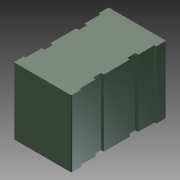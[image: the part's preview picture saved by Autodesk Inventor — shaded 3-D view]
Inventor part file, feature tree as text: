
AUTODESK INVENTOR PART (.ipt)
format: ipt  version: 2011 SP1 (Build 150282100, 282)  size: 150,016 bytes
history: native  units: in
note: dims shown in document units (in); Inventor stores cm internally (conversion verified against a paired STEP export)
features: other x21, extrude x3, sketch x3, pattern_linear x1
ambient origin geometry x8: Origin, YZ Plane, XZ Plane, XY Plane, X Axis, Y Axis, Z Axis, Center Point
bodies: Solid1 (feature_tree)
feature tree (28):
  extrude  "Extrusion1"  Depth=0.001in TaperAngle=0.0deg
  extrude  "Extrusion2"  Depth=1.1811in TaperAngle=0.0deg
  extrude  "Extrusion3"  [1 undecoded]
  pattern_linear  "Rectangular Pattern1"  [2 undecoded]
  other  "rot_XY"
  other  "rot_YZ"
  other  "rot_ZX"
  other  "rot_X"
  other  "rot_Y"
  other  "rot_Z"
  other  "rot_Center"
  other  "to_cover_XY"
  other  "to_cover_YZ"
  other  "to_cover_ZX"
  other  "to_cover_X"
  other  "to_cover_Y"
  other  "to_cover_Z"
  other  "to_cover_Center"
  other  "to_terminals_XY"
  other  "to_terminals_YZ"
  other  "to_terminals_ZX"
  other  "to_terminals_X"
  other  "to_terminals_Y"
  other  "to_terminals_Z"
  other  "to_terminals_Center"
  sketch  "Sketch_2"  dims[d4=0.01in d5=0.0in d6=1.1811in d8=0.185in d9=0.3937in d11=0.0in]
  sketch  "Sketch_1"  dims[d0=0.361in d1=0.0in d2=0.001in d3=0.0in]
  sketch  "Sketch_7"
note: 3 required parameter values undecoded (feature->parameter linkage not recoverable at this tier; creation-order binding heuristic only, values carry confidence <= 0.55)
